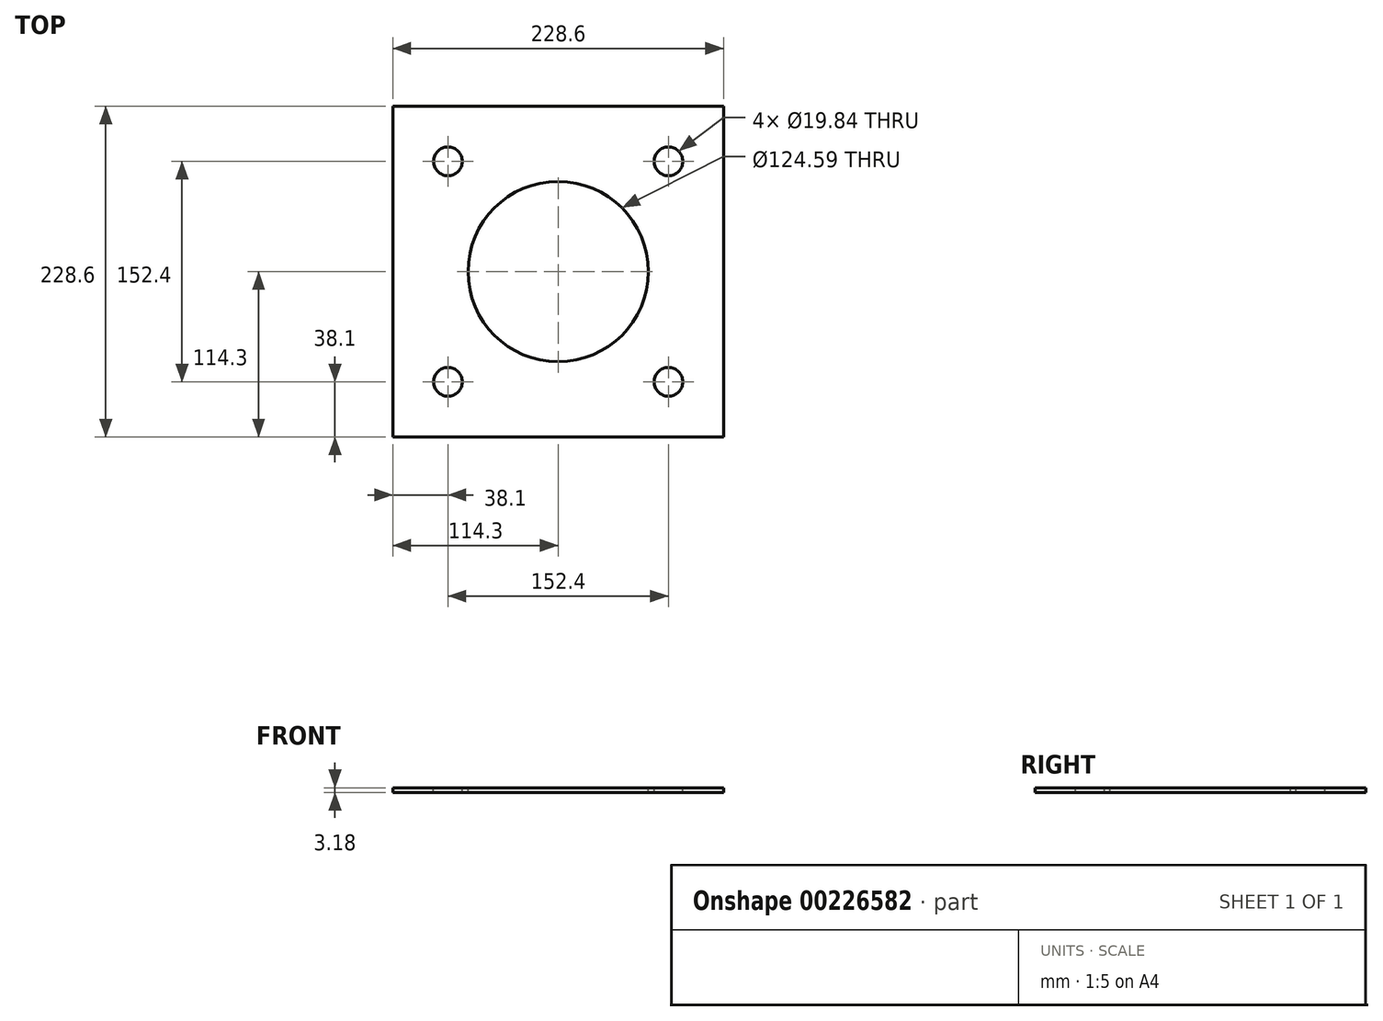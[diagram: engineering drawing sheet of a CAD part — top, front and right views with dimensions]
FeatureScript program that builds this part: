
annotation { "Feature Type Name" : "Feature", "Feature Type Description" : "" }
export const myFeature = defineFeature(function(context is Context, id is Id, definition is map)
    precondition{}
    {
        {
            var Q0;
            Q0=qCreatedBy(makeId("Top.planeOp"),FACE);
            var sketch = newSketch(context, id + "F0", { "sketchPlane" : qUnion([Q0])});
            skLineSegment(sketch, "E0.bottom", {"start": v(114.3, 114.3) * mm, "end": v(-114.3, 114.3) * mm});
            skLineSegment(sketch, "E0.top", {"start": v(114.3, -114.3) * mm, "end": v(-114.3, -114.3) * mm});
            skLineSegment(sketch, "E0.left", {"start": v(114.3, 114.3) * mm, "end": v(114.3, -114.3) * mm});
            skLineSegment(sketch, "E0.right", {"start": v(-114.3, 114.3) * mm, "end": v(-114.3, -114.3) * mm});
            skPoint(sketch, "E0.middle", {"position": v(0, 0) * mm});
            skSolve(sketch);
        }
        {
            var Q0;
            Q0=qSketchRegion(id+"F0",true);
            extrude(context, id + "F1", {"entities" : qUnion([Q0]), "oppositeDirection" : true, "depth" : 3.17 * mm, "symmetric" : true});
        }
        {
            var Q0;
            Q0=makeQuery(id+"F1.opExtrude","CAP_FACE",FACE,{"disambiguationData":[OSD([sQuery(id+"F0.wireOp",EDGE,"E0.bottom"),sQuery(id+"F0.wireOp",EDGE,"E0.top"),sQuery(id+"F0.wireOp",EDGE,"E0.left"),sQuery(id+"F0.wireOp",EDGE,"E0.right")])],"isStart":true});
            var sketch = newSketch(context, id + "F2", { "sketchPlane" : qUnion([Q0])});
            skLineSegment(sketch, "E1.bottom", {"start": v(76.2, 76.2) * mm, "end": v(-76.2, 76.2) * mm});
            skLineSegment(sketch, "E1.top", {"start": v(76.2, -76.2) * mm, "end": v(-76.2, -76.2) * mm});
            skLineSegment(sketch, "E1.left", {"start": v(76.2, 76.2) * mm, "end": v(76.2, -76.2) * mm});
            skLineSegment(sketch, "E1.right", {"start": v(-76.2, 76.2) * mm, "end": v(-76.2, -76.2) * mm});
            skPoint(sketch, "E1.middle", {"position": v(0, 0) * mm});
            skSolve(sketch);
        }
        {
            var Q0;
            Q0=sQuery(id+"F2.wireOp",VERTEX,"E1.right.start");
            var Q1;
            Q1=sQuery(id+"F2.wireOp",VERTEX,"E1.left.start");
            var Q2;
            Q2=sQuery(id+"F2.wireOp",VERTEX,"E1.top.end");
            var Q3;
            Q3=sQuery(id+"F2.wireOp",VERTEX,"E1.left.end");
            var Q4;
            Q4=makeQuery(id+"F1.opExtrude","SWEPT_BODY",BODY,{"disambiguationData":[OSD([sQuery(id+"F0.wireOp",EDGE,"E0.bottom"),sQuery(id+"F0.wireOp",EDGE,"E0.top"),sQuery(id+"F0.wireOp",EDGE,"E0.left"),sQuery(id+"F0.wireOp",EDGE,"E0.right")])]});
            hole(context, id + "F3", {"style" : HoleStyle.SIMPLE, "endStyle" : HoleEndStyle.THROUGH, "standardTappedOrClearance" : lookupTablePath({ "standard" : "ANSI", "fit" : "Normal (ASME)", "size" : "3/4", "type" : "Clearance" }), "standardBlindInLast" : lookupTablePath({ "fit" : "Free", "standard" : "ANSI", "size" : "3/4", "type" : "Clearance" }), "holeDiameter" : 19.84 * mm, "locations" : qUnion([Q0, Q1, Q2, Q3]), "scope" : qUnion([Q4]), "isTappedThrough" : true});
        }
        {
            var Q0;
            Q0=sQuery(id+"F2.wireOp",VERTEX,"E1.middle");
            var Q1;
            Q1=makeQuery(id+"F1.opExtrude","SWEPT_BODY",BODY,{"disambiguationData":[OSD([sQuery(id+"F0.wireOp",EDGE,"E0.bottom"),sQuery(id+"F0.wireOp",EDGE,"E0.top"),sQuery(id+"F0.wireOp",EDGE,"E0.left"),sQuery(id+"F0.wireOp",EDGE,"E0.right")])]});
            hole(context, id + "F4", {"style" : HoleStyle.SIMPLE, "endStyle" : HoleEndStyle.THROUGH, "holeDiameter" : 124.6 * mm, "locations" : qUnion([Q0]), "scope" : qUnion([Q1]), "isTappedThrough" : true});
        }
    });
